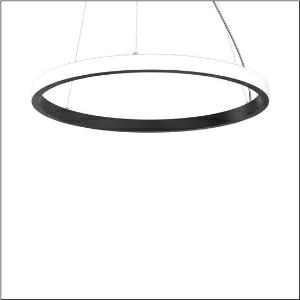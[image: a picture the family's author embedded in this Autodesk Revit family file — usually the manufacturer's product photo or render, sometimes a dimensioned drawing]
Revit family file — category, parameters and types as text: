
# Revit family: silica_r__21_ring-o_5pjbo4d3104a_8b26
name_source: partatom
category: Lighting Fixtures
units: mm (PartAtom-declared; Revit-internal decimal feet)

## family parameters
Cut with Voids When Loaded = No
Host = Face
Light Source = No
Part Type = Normal
Room Calculation Point = No
Round Connector Dimension = Use Diameter
Shared = No

## types (1)
- Silica® 21 Ring-O (1 x LED, 9260 lm, 140 W, 4000K)
    Apparent Load = 140 VA
    CIE Flux Codes = 2 16 49 50 100
    Color Rendering = 80
    Color Temperature = 4000K
    Default Elevation = 1800 mm
    Description = Silica® 21 Ring-O, suspended luminaire, of PMMA, frosted, light emission: outer ring side luminous distribution, primary light characteristic: symmetric, installation type: suspended mounting, LED, rated luminous flux: 9.260lm, luminous efficacy: 66lm/W, light colour: 840, colour temperature: 4000K, with terminal, 5-pole, mains connection: 230V, AC/DC, 0/50..60Hz, rated input power: 140W, housing, of extruded aluminium section, jet black (RAL 9005), diameter: 1.480mm, ceiling canopy, jet black (RAL 9005), protection rating (lamp compartment): IP40, insulation class (complete): insulation class I (protective earthing), certification: CE, impact resistance: IK02, permissible operating ambient temperature: 0..+35°C, packaging unit: 1 piece
    Height = 48 mm  [stored 0.15748 ft]
    Lamp = 1 x LED
    Lamp Light Flux = 9260 lm
    Lamp Power = 140 W
    Lamp count = 1
    Length = 1480 mm
    Luminous efficacy = 66 lm/W
    Manufacturer = Siteco
    ModVariant = No
    Model = 5PJBO4D3104A
    Mounting Place = Ceiling
    Mounting Type = Pendant
    Number of Poles = 1
    OnlyDefault = Yes
    Power Factor = 1
    Product Name = Silica® 21 Ring-O
    Product group = suspended luminaire
    ProductGroupID = 904
    Protection Class = Protection class I
    Protection Degree = Degree of protection
    RLX_Detail_Level = 1
    RLX_Emergency_Light_Flux = 0 lm
    RLX_Emergency_Type = 0
    RLX_Emergency_Type_DB = No
    RlxData = <blob elided: 20537 chars, md5=5c679cf4>
    Socket = socket
    Standby Power = 0 W
    System Light Flux = 9260 lm
    System Power = 140 W
    Type Comments = Product without accessories
    Type Image = l_1258389.jpg
    URL = http://relux.com
    VarID = ---
    Voltage = 0 V
    Weight = 0.00 kg
    Width = 0 mm  [stored 0 ft]

note: [stored X ft] marks values corroborated as IEEE doubles in the binary element streams (Revit-internal decimal feet)

## geometry (parser evidence)
native form markers: Blend x4, Sweep x12
no freeform markers — native parametric forms only
